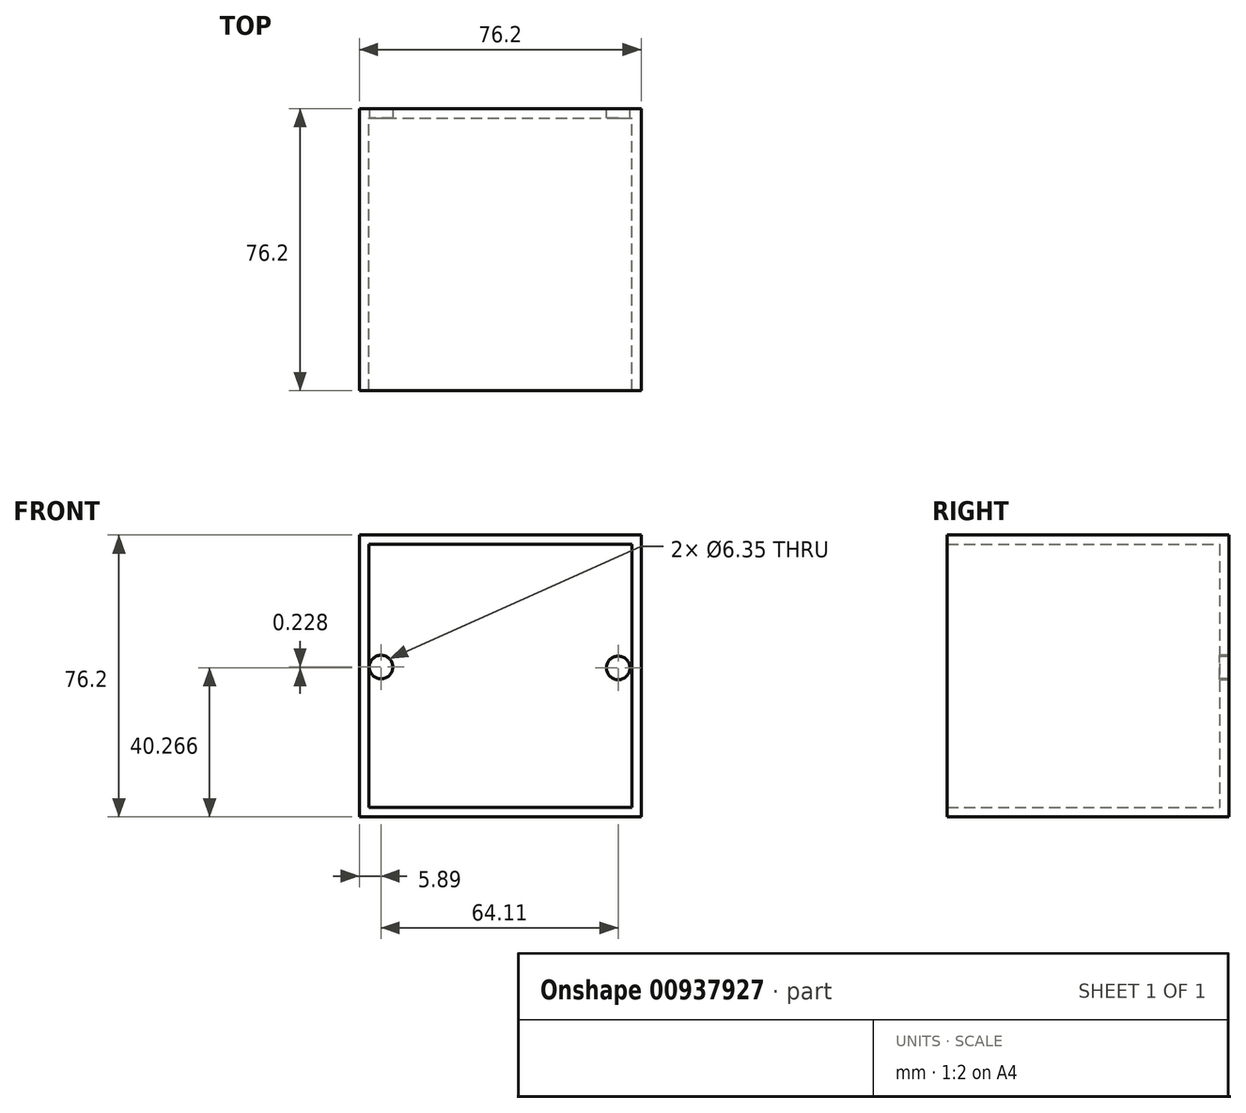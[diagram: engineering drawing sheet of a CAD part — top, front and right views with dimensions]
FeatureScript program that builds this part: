
annotation { "Feature Type Name" : "Feature", "Feature Type Description" : "" }
export const myFeature = defineFeature(function(context is Context, id is Id, definition is map)
    precondition{}
    {
        {
            var Q0;
            Q0=qCreatedBy(makeId("Front.planeOp"),FACE);
            var sketch = newSketch(context, id + "F0", { "sketchPlane" : qUnion([Q0])});
            skLineSegment(sketch, "E0.bottom", {"start": v(0, 0) * mm, "end": v(76.2, 0) * mm});
            skLineSegment(sketch, "E0.top", {"start": v(0, -76.2) * mm, "end": v(76.2, -76.2) * mm});
            skLineSegment(sketch, "E0.left", {"start": v(0, 0) * mm, "end": v(0, -76.2) * mm});
            skLineSegment(sketch, "E0.right", {"start": v(76.2, 0) * mm, "end": v(76.2, -76.2) * mm});
            skSolve(sketch);
        }
        {
            var Q0;
            Q0=makeQuery(id+"F0.imprint","IMPRINT",FACE,{"disambiguationData":[TD([[makeQuery(id+"F0.imprint","IMPRINT",EDGE,{"derivedFrom":sQuery(id+"F0.wireOp",EDGE,"E0.bottom")}),-1.0]])]});
            extrude(context, id + "F1", {"entities" : qUnion([Q0]), "depth" : 76.2 * mm, "offsetDistance" : 25.4 * mm});
        }
        {
            var Q0;
            Q0=makeQuery(id+"F1.opExtrude","CAP_FACE",FACE,{"disambiguationData":[OSD([sQuery(id+"F0.wireOp",EDGE,"E0.bottom"),sQuery(id+"F0.wireOp",EDGE,"E0.top"),sQuery(id+"F0.wireOp",EDGE,"E0.left"),sQuery(id+"F0.wireOp",EDGE,"E0.right")])],"isStart":false});
            shell(context, id + "F2", {"entities" : qUnion([Q0]), "thickness" : 2.54 * mm});
        }
        {
            var Q0;
            Q0=makeQuery(id+"F1.opExtrude","CAP_FACE",FACE,{"disambiguationData":[OSD([sQuery(id+"F0.wireOp",EDGE,"E0.bottom"),sQuery(id+"F0.wireOp",EDGE,"E0.top"),sQuery(id+"F0.wireOp",EDGE,"E0.left"),sQuery(id+"F0.wireOp",EDGE,"E0.right")])],"isStart":true});
            var sketch = newSketch(context, id + "F3", { "sketchPlane" : qUnion([Q0])});
            skCircle(sketch, "E1", {"center": v(-70, -35.93) * mm, "radius": 4.16 * mm});
            skSolve(sketch);
        }
        {
            var Q0;
            Q0=sQuery(id+"F3.wireOp",VERTEX,"E1.center");
            var Q1;
            Q1=makeQuery(id+"F1.opExtrude","SWEPT_BODY",BODY,{"disambiguationData":[OSD([sQuery(id+"F0.wireOp",EDGE,"E0.bottom"),sQuery(id+"F0.wireOp",EDGE,"E0.top"),sQuery(id+"F0.wireOp",EDGE,"E0.left"),sQuery(id+"F0.wireOp",EDGE,"E0.right")])]});
            hole(context, id + "F4", {"style" : HoleStyle.SIMPLE, "endStyle" : HoleEndStyle.THROUGH, "holeDiameter" : 6.35 * mm, "majorDiameter" : 6.35 * mm, "isTappedThrough" : true, "tappedDepth" : 12.7 * mm, "tapClearance" : 3, "locations" : qUnion([Q0]), "scope" : qUnion([Q1])});
        }
        {
            var Q0;
            Q0=makeQuery(id+"F2.opShell","OFFSET_FACE",FACE,{"disambiguationData":[OSD([sQuery(id+"F0.wireOp",EDGE,"E0.bottom"),sQuery(id+"F0.wireOp",EDGE,"E0.top"),sQuery(id+"F0.wireOp",EDGE,"E0.left"),sQuery(id+"F0.wireOp",EDGE,"E0.right")])]});
            var sketch = newSketch(context, id + "F5", { "sketchPlane" : qUnion([Q0])});
            skLineSegment(sketch, "E2", {"start": v(66.83, -35.7) * mm, "end": v(10.11, -35.7) * mm});
            skCircle(sketch, "E3", {"center": v(5.89, -35.7) * mm, "radius": 2.95 * mm});
            skSolve(sketch);
        }
        {
            var Q0;
            Q0=sQuery(id+"F5.wireOp",VERTEX,"E3.center");
            var Q1;
            Q1=makeQuery(id+"F1.opExtrude","SWEPT_BODY",BODY,{"disambiguationData":[OSD([sQuery(id+"F0.wireOp",EDGE,"E0.bottom"),sQuery(id+"F0.wireOp",EDGE,"E0.top"),sQuery(id+"F0.wireOp",EDGE,"E0.left"),sQuery(id+"F0.wireOp",EDGE,"E0.right")])]});
            hole(context, id + "F6", {"style" : HoleStyle.SIMPLE, "endStyle" : HoleEndStyle.THROUGH, "holeDiameter" : 6.35 * mm, "majorDiameter" : 6.35 * mm, "isTappedThrough" : true, "tappedDepth" : 12.7 * mm, "tapClearance" : 3, "locations" : qUnion([Q0]), "scope" : qUnion([Q1])});
        }
    });
